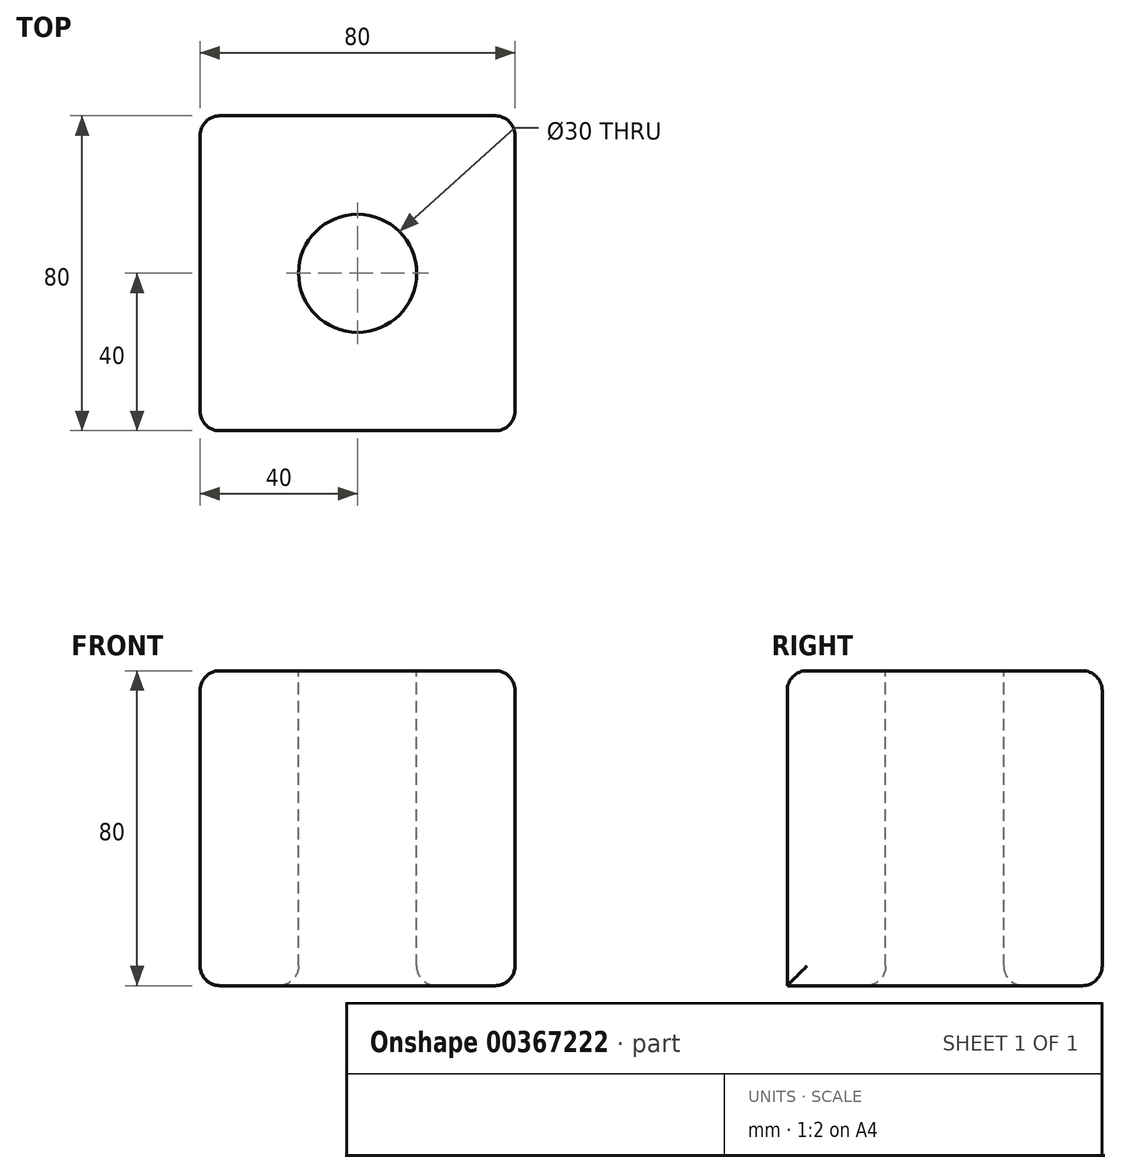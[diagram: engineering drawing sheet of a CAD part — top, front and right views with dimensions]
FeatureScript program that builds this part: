
annotation { "Feature Type Name" : "Feature", "Feature Type Description" : "" }
export const myFeature = defineFeature(function(context is Context, id is Id, definition is map)
    precondition{}
    {
        {
            var Q0;
            Q0=qCreatedBy(makeId("Top.planeOp"),FACE);
            var sketch = newSketch(context, id + "F0", { "sketchPlane" : qUnion([Q0])});
            skLineSegment(sketch, "E0.bottom", {"start": v(-40, 40) * mm, "end": v(40, 40) * mm});
            skLineSegment(sketch, "E0.top", {"start": v(-40, -40) * mm, "end": v(40, -40) * mm});
            skLineSegment(sketch, "E0.left", {"start": v(-40, 40) * mm, "end": v(-40, -40) * mm});
            skLineSegment(sketch, "E0.right", {"start": v(40, 40) * mm, "end": v(40, -40) * mm});
            skPoint(sketch, "E0.middle", {"position": v(0, 0) * mm});
            skSolve(sketch);
        }
        {
            var Q0;
            Q0 = qSketchRegion(id + "F0", true);
            extrude(context, id + "F1", {"entities" : qUnion([Q0]), "depth" : 80 * mm});
        }
        {
            var Q0;
            Q0=makeQuery(id+"F1.opExtrude","CAP_FACE",FACE,{"disambiguationData":[OSD([sQuery(id+"F0.wireOp",EDGE,"E0.bottom"),sQuery(id+"F0.wireOp",EDGE,"E0.top"),sQuery(id+"F0.wireOp",EDGE,"E0.left"),sQuery(id+"F0.wireOp",EDGE,"E0.right")])],"isStart":false});
            var sketch = newSketch(context, id + "F2", { "sketchPlane" : qUnion([Q0])});
            skCircle(sketch, "E1", {"center": v(0, 0) * mm, "radius": 15 * mm});
            skSolve(sketch);
        }
        {
            var Q0;
            Q0=makeQuery(id+"F2.imprint","IMPRINT",FACE,{"disambiguationData":[TD([[makeQuery(id+"F2.imprint","IMPRINT",EDGE,{"derivedFrom":sQuery(id+"F2.wireOp",EDGE,"E1")}),1.0]])]});
            extrude(context, id + "F3", {"entities" : qUnion([Q0]), "operationType" : NewBodyOperationType.REMOVE, "endBound" : BoundingType.THROUGH_ALL, "oppositeDirection" : true, "depth" : 25 * mm});
        }
        {
            var Q0;
            Q0=makeQuery(id+"F1.opExtrude","SWEPT_EDGE",EDGE,{"disambiguationData":[OSD([sQuery(id+"F0.wireOp",EDGE,"E0.top"),sQuery(id+"F0.wireOp",EDGE,"E0.left")])]});
            var Q1;
            Q1=makeQuery(id+"F1.opExtrude","CAP_EDGE",EDGE,{"disambiguationData":[OSD([sQuery(id+"F0.wireOp",EDGE,"E0.top")])],"isStart":false});
            var Q2;
            Q2=makeQuery(id+"F1.opExtrude","SWEPT_EDGE",EDGE,{"disambiguationData":[OSD([sQuery(id+"F0.wireOp",EDGE,"E0.top"),sQuery(id+"F0.wireOp",EDGE,"E0.right")])]});
            var Q3;
            Q3=makeQuery(id+"F1.opExtrude","SWEPT_FACE",FACE,{"disambiguationData":[OSD([sQuery(id+"F0.wireOp",EDGE,"E0.right")])]});
            var Q4;
            Q4=makeQuery(id+"F1.opExtrude","SWEPT_EDGE",EDGE,{"disambiguationData":[OSD([sQuery(id+"F0.wireOp",EDGE,"E0.bottom"),sQuery(id+"F0.wireOp",EDGE,"E0.right")])]});
            var Q5;
            Q5=makeQuery(id+"F1.opExtrude","CAP_EDGE",EDGE,{"disambiguationData":[OSD([sQuery(id+"F0.wireOp",EDGE,"E0.left")])],"isStart":false});
            var Q6;
            Q6=makeQuery(id+"F1.opExtrude","CAP_EDGE",EDGE,{"disambiguationData":[OSD([sQuery(id+"F0.wireOp",EDGE,"E0.left")])],"isStart":true});
            var Q7;
            Q7=makeQuery(id+"F1.opExtrude","CAP_EDGE",EDGE,{"disambiguationData":[OSD([sQuery(id+"F0.wireOp",EDGE,"E0.right")])],"isStart":true});
            var Q8;
            Q8=makeQuery(id+"F1.opExtrude","SWEPT_FACE",FACE,{"disambiguationData":[OSD([sQuery(id+"F0.wireOp",EDGE,"E0.bottom")])]});
            fillet(context, id + "F4", {"entities" : qUnion([Q0, Q1, Q2, Q3, Q4, Q5, Q6, Q7, Q8]), "radius" : 5 * mm, "tangentPropagation" : true, "allowEdgeOverflow" : false});
        }
        {
            var Q0;
            Q0=makeQuery(id+"F3.boolean.opBoolean","COPY",EDGE,{"derivedFrom":makeQuery(id+"F3.opExtrude","CAP_EDGE",EDGE,{"disambiguationData":[OSD([sQuery(id+"F2.wireOp",EDGE,"E1")])],"isStart":true})});
            var Q1;
            Q1=makeQuery(id+"F3.boolean.opBoolean","INTERSECT",EDGE,{"derivedFrom":[makeQuery(id+"F1.opExtrude","CAP_FACE",FACE,{"disambiguationData":[OSD([sQuery(id+"F0.wireOp",EDGE,"E0.bottom"),sQuery(id+"F0.wireOp",EDGE,"E0.top"),sQuery(id+"F0.wireOp",EDGE,"E0.left"),sQuery(id+"F0.wireOp",EDGE,"E0.right")])],"isStart":true}),makeQuery(id+"F3.opExtrude","SWEPT_FACE",FACE,{"disambiguationData":[OSD([sQuery(id+"F2.wireOp",EDGE,"E1")])]})]});
            fillet(context, id + "F5", {"entities" : qUnion([Q0, Q1]), "radius" : 5 * mm, "tangentPropagation" : true, "allowEdgeOverflow" : false});
        }
    });
